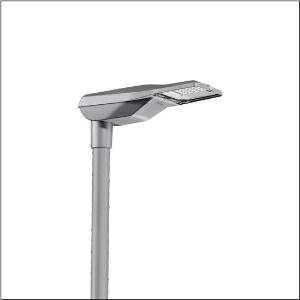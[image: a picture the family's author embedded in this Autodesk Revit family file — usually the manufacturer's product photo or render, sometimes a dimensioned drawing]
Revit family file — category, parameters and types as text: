
# Revit family: streetlight_sl_21_iq_micro___stw1_0a_5xe1e21d08cb_e74e
name_source: partatom
category: Lighting Fixtures
units: mm (PartAtom-declared; Revit-internal decimal feet)

## family parameters
Cut with Voids When Loaded = No
Host = Face
Light Source = No
Part Type = Normal
Room Calculation Point = No
Round Connector Dimension = Use Diameter
Shared = No

## types (1)
- --- (1 x LED, 2380 lm, 19.4 W, 2200K)
    Apparent Load = 19 VA
    CIE Flux Codes = 38 75 98 100 100
    Color Rendering = 70
    Color Temperature = 2200K
    Default Elevation = 1800 mm
    Description = Streetlight SL 21 iQ micro, mast luminaire, primary light control with lens, of PMMA, primary optical cover: cover, of toughened safety glass, transparent, light distribution: STW1.0a, light emission: direct distribution, primary light characteristic: asymmetric, installation type: post-top, side-entry, LED, High Power LED, rated luminous flux: 2.380lm, luminous efficacy: 123lm/W, light colour: 722, colour temperature: 2200K, control: Auto-Match, Temp-Guard, Lumen-Switch, Night-Set, Smart-Wire, Light-Fading, Desk-Remote (wireless, voltage-free reading and setting of iQ features in the workshop via application-optimized NFC function/RFID function), optimised constant luminous flux control (CLO 2.0), presetting dimming linear, mains connection: 220..240V, AC, 50/60Hz, start of lifetime: 19W, end of service life: 20W, reduction: 10W, luminaire housing, of diecast aluminium, powder-coated, Siteco® metallic grey (DB 702S), corrosivity category C5 mid according to DIN EN ISO 12944, please order mast flange separately, inclination adjustable: 0°, 5°, 10°, 15°, sealing non-destructively replaceable, multi-level sealing system, length: 528mm, width: 235mm, height: 110mm, mast flange for spigot size: 42mm (side-entry): 5XC10008XM4, 60/48mm (side-entry/post-top): 5XC10108XM2, 76/60mm (side-entry/post-top): 5XC10108XM1, protection rating (complete): IP66, insulation class (complete): insulation class II (safety insulation), certification: CE, ENEC, ENEC+, VDE, impact resistance: IK09, permissible operating ambient temperature for outdoor applications: -40..+50°C, standard-compliant lighting for roads and squares, packaging unit: 1 piece

Light Distribution: STW1.0a
    Height = 110 mm
    Lamp = 1 x LED
    Lamp Light Flux = 2380 lm
    Lamp Power = 19.4 W
    Lamp count = 1
    Length = 528 mm
    Luminous efficacy = 123 lm/W
    Manufacturer = Siteco
    ModVariant = No
    Model = 5XE1E21D08CB
    Number of Poles = 1
    OnlyDefault = Yes
    Power Factor = 1
    Product Name = Streetlight SL 21 iQ micro | STW1.0a
    Product group = mast luminaire | pylon top
    ProductGroupID = 6100
    Protection Class = Protection class II
    Protection Degree = IP 66
    RLX_Detail_Level = 1
    RLX_Emergency_Light_Flux = 0 lm
    RLX_Emergency_Type = 0
    RLX_Emergency_Type_DB = No
    RlxData = <blob elided: 98601 chars, md5=6604d178>
    Socket = socket
    Standby Power = 0 W
    System Light Flux = 2380 lm
    System Power = 19 W
    Type Comments = factory setting: luminous flux: 100 % | dim-lin: 254 | 387 mA
    Type Image = l_1006881.jpg
    URL = http://relux.com
    VarID = @adj_070293
    Voltage = 0 V
    Weight = 0.00 kg
    Width = 235 mm

## geometry (parser evidence)
native form markers: Blend x4, Sweep x11
no freeform markers — native parametric forms only
